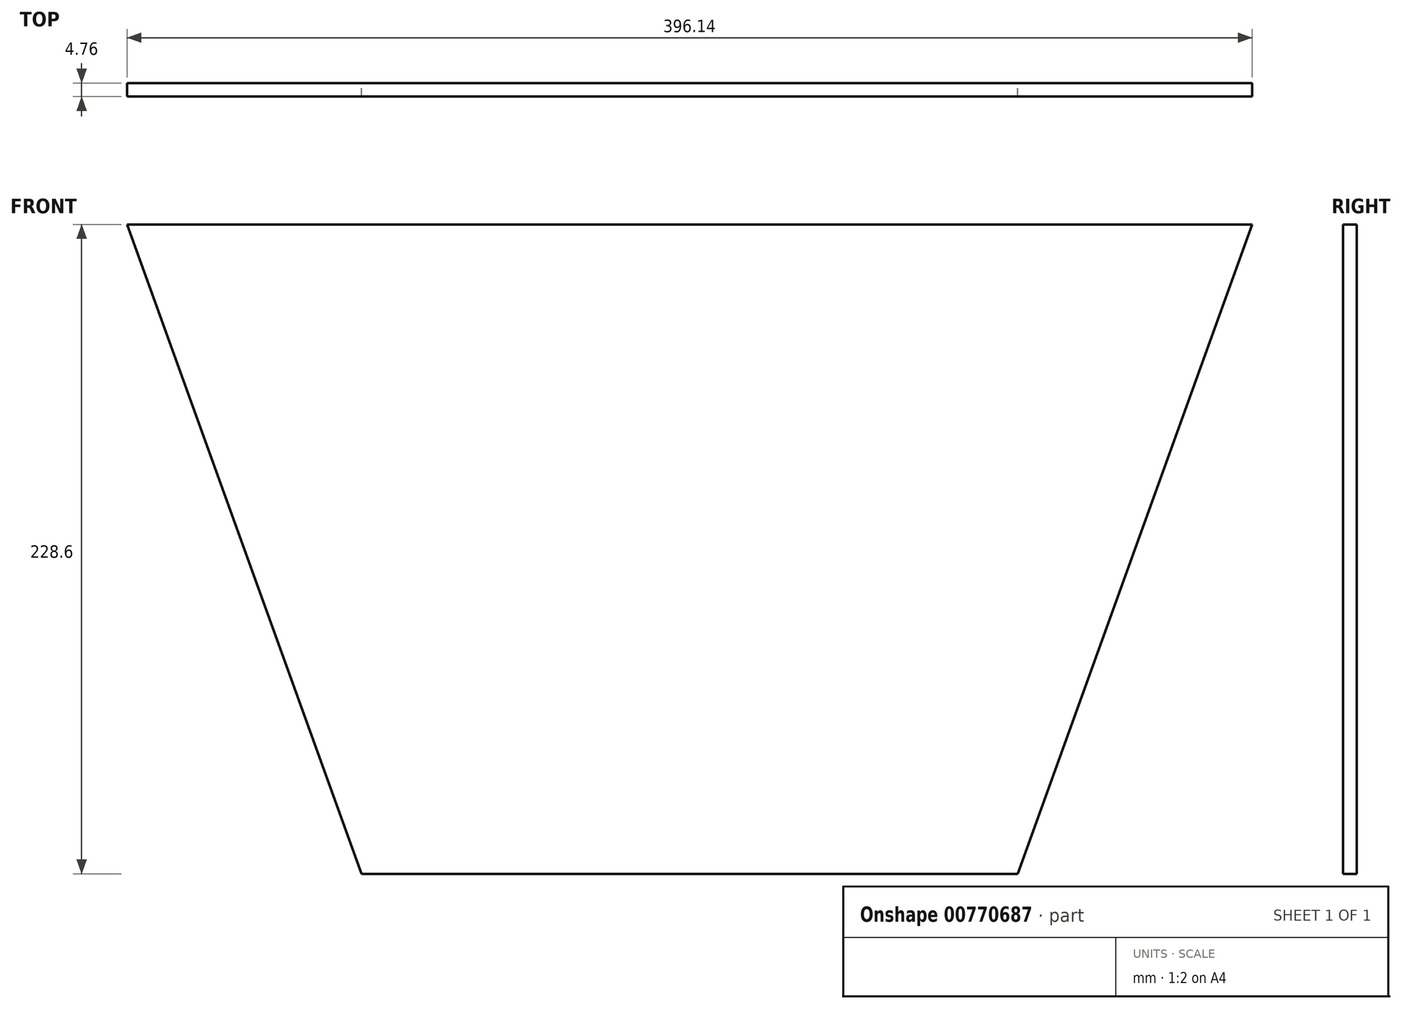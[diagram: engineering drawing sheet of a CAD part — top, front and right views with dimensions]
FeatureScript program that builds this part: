
annotation { "Feature Type Name" : "Feature", "Feature Type Description" : "" }
export const myFeature = defineFeature(function(context is Context, id is Id, definition is map)
    precondition{}
    {
        {
            var Q0;
            Q0=qCreatedBy(makeId("Front.planeOp"),FACE);
            var sketch = newSketch(context, id + "F0", { "sketchPlane" : qUnion([Q0])});
            skLineSegment(sketch, "E0", {"start": v(-198.07, 204.74) * mm, "end": v(-115.54, -23.86) * mm});
            skLineSegment(sketch, "E1", {"start": v(-115.54, -23.86) * mm, "end": v(115.54, -23.86) * mm});
            skLineSegment(sketch, "E2", {"start": v(115.54, -23.86) * mm, "end": v(198.07, 204.74) * mm});
            skLineSegment(sketch, "E3", {"start": v(-198.07, 204.74) * mm, "end": v(198.07, 204.74) * mm});
            skSolve(sketch);
        }
        {
            var Q0;
            Q0=makeQuery(id+"F0.imprint","IMPRINT",FACE,{"disambiguationData":[TD([[makeQuery(id+"F0.imprint","IMPRINT",EDGE,{"derivedFrom":sQuery(id+"F0.wireOp",EDGE,"E0")}),1.0]])]});
            extrude(context, id + "F1", {"entities" : qUnion([Q0]), "endBound" : BoundingType.SYMMETRIC, "depth" : 4.76 * mm, "offsetDistance" : 25.4 * mm});
        }
    });
